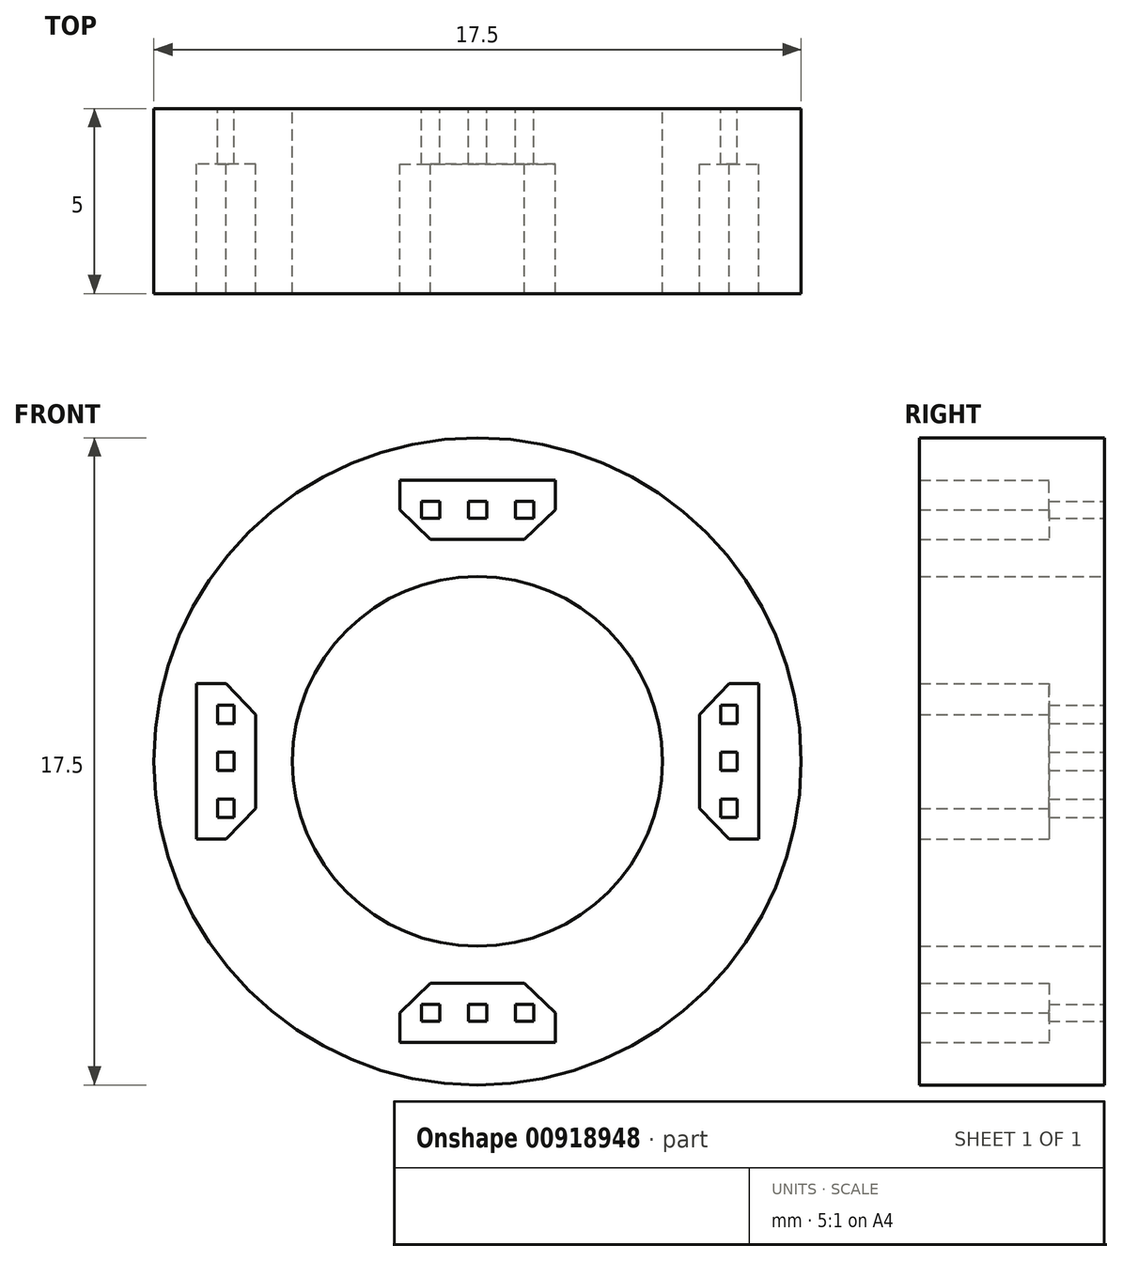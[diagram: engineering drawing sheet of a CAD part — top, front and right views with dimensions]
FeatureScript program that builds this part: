
annotation { "Feature Type Name" : "Feature", "Feature Type Description" : "" }
export const myFeature = defineFeature(function(context is Context, id is Id, definition is map)
    precondition{}
    {
        {
            var Q0;
            Q0=qCreatedBy(makeId("Front.planeOp"),FACE);
            var sketch = newSketch(context, id + "F0", { "sketchPlane" : qUnion([Q0])});
            skLineSegment(sketch, "E0", {"start": v(-2.1, 7.6) * mm, "end": v(2.1, 7.6) * mm});
            skLineSegment(sketch, "E1", {"start": v(2.1, 7.6) * mm, "end": v(2.1, 6.8) * mm});
            skLineSegment(sketch, "E2", {"start": v(2.1, 6.8) * mm, "end": v(1.27, 6) * mm});
            skLineSegment(sketch, "E3", {"start": v(1.27, 6) * mm, "end": v(-1.27, 6) * mm});
            skLineSegment(sketch, "E4", {"start": v(-1.27, 6) * mm, "end": v(-2.1, 6.8) * mm});
            skLineSegment(sketch, "E5", {"start": v(-2.1, 6.8) * mm, "end": v(-2.1, 7.6) * mm});
            skPoint(sketch, "E6", {"position": v(0, 7.6) * mm});
            skPoint(sketch, "E7", {"position": v(0, 6) * mm});
            skLineSegment(sketch, "E8", {"start": v(-2.1, 6.8) * mm, "end": v(2.1, 6.8) * mm, "construction": true});
            skLineSegment(sketch, "E9", {"start": v(0, 7.6) * mm, "end": v(0, 6) * mm, "construction": true});
            skPoint(sketch, "E10", {"position": v(0, 6.8) * mm});
            skLineSegment(sketch, "E11.bottom", {"start": v(0.25, 6.58) * mm, "end": v(-0.25, 6.58) * mm});
            skLineSegment(sketch, "E11.top", {"start": v(0.25, 7.03) * mm, "end": v(-0.25, 7.03) * mm});
            skLineSegment(sketch, "E11.left", {"start": v(0.25, 6.58) * mm, "end": v(0.25, 7.03) * mm});
            skLineSegment(sketch, "E11.right", {"start": v(-0.25, 6.58) * mm, "end": v(-0.25, 7.03) * mm});
            skLineSegment(sketch, "E12", {"start": v(1.27, 6) * mm, "end": v(1.27, 7.6) * mm, "construction": true});
            skPoint(sketch, "E13", {"position": v(1.27, 6.8) * mm});
            skLineSegment(sketch, "E14", {"start": v(-1.27, 6) * mm, "end": v(-1.27, 7.6) * mm, "construction": true});
            skPoint(sketch, "E15", {"position": v(-1.27, 6.8) * mm});
            skLineSegment(sketch, "E16", {"start": v(-1.52, 7.03) * mm, "end": v(-1.02, 7.03) * mm});
            skLineSegment(sketch, "E17", {"start": v(-1.02, 7.03) * mm, "end": v(-1.02, 6.58) * mm});
            skLineSegment(sketch, "E18", {"start": v(-1.02, 6.58) * mm, "end": v(-1.52, 6.58) * mm});
            skLineSegment(sketch, "E19", {"start": v(-1.52, 6.58) * mm, "end": v(-1.52, 7.03) * mm});
            skPoint(sketch, "E20", {"position": v(-1.27, 7.03) * mm});
            skLineSegment(sketch, "E21", {"start": v(1.52, 7.03) * mm, "end": v(1.52, 6.58) * mm});
            skLineSegment(sketch, "E22", {"start": v(1.52, 6.58) * mm, "end": v(1.02, 6.58) * mm});
            skLineSegment(sketch, "E23", {"start": v(1.02, 6.58) * mm, "end": v(1.02, 7.03) * mm});
            skLineSegment(sketch, "E24", {"start": v(1.02, 7.03) * mm, "end": v(1.52, 7.03) * mm});
            skPoint(sketch, "E25", {"position": v(1.27, 7.03) * mm});
            skPoint(sketch, "E26.1.0", {"position": v(-6.8, 1.27) * mm});
            skLineSegment(sketch, "E26.1.1", {"start": v(-6, 1.27) * mm, "end": v(-6, -1.27) * mm});
            skPoint(sketch, "E26.1.2", {"position": v(-7.03, 1.27) * mm});
            skLineSegment(sketch, "E26.1.3", {"start": v(-7.6, -2.1) * mm, "end": v(-7.6, 2.1) * mm});
            skPoint(sketch, "E26.1.4", {"position": v(-6, 0) * mm});
            skLineSegment(sketch, "E26.1.5", {"start": v(-6.8, 2.1) * mm, "end": v(-6, 1.27) * mm});
            skPoint(sketch, "E26.1.6", {"position": v(-7.6, 0) * mm});
            skLineSegment(sketch, "E26.1.7", {"start": v(-6, -1.27) * mm, "end": v(-6.8, -2.1) * mm});
            skPoint(sketch, "E26.1.8", {"position": v(-7.03, -1.27) * mm});
            skPoint(sketch, "E26.1.9", {"position": v(-6.8, -1.27) * mm});
            skLineSegment(sketch, "E26.1.10", {"start": v(-6.8, -2.1) * mm, "end": v(-7.6, -2.1) * mm});
            skLineSegment(sketch, "E26.1.11", {"start": v(-6, -1.27) * mm, "end": v(-7.6, -1.27) * mm, "construction": true});
            skLineSegment(sketch, "E26.1.12", {"start": v(-6, 1.27) * mm, "end": v(-7.6, 1.27) * mm, "construction": true});
            skLineSegment(sketch, "E26.1.13", {"start": v(-7.6, 2.1) * mm, "end": v(-6.8, 2.1) * mm});
            skPoint(sketch, "E26.1.14", {"position": v(-6.8, 0) * mm});
            skLineSegment(sketch, "E26.1.15", {"start": v(-6.8, -2.1) * mm, "end": v(-6.8, 2.1) * mm, "construction": true});
            skLineSegment(sketch, "E26.1.16", {"start": v(-7.6, 0) * mm, "end": v(-6, 0) * mm, "construction": true});
            skLineSegment(sketch, "E26.1.17", {"start": v(-6.58, -1.02) * mm, "end": v(-6.58, -1.52) * mm});
            skLineSegment(sketch, "E26.1.18", {"start": v(-7.03, -1.52) * mm, "end": v(-7.03, -1.02) * mm});
            skLineSegment(sketch, "E26.1.19", {"start": v(-6.58, 1.52) * mm, "end": v(-6.58, 1.02) * mm});
            skLineSegment(sketch, "E26.1.20", {"start": v(-7.03, -1.02) * mm, "end": v(-6.58, -1.02) * mm});
            skLineSegment(sketch, "E26.1.21", {"start": v(-6.58, 1.02) * mm, "end": v(-7.03, 1.02) * mm});
            skLineSegment(sketch, "E26.1.22", {"start": v(-7.03, 1.52) * mm, "end": v(-6.58, 1.52) * mm});
            skLineSegment(sketch, "E26.1.23", {"start": v(-7.03, 1.02) * mm, "end": v(-7.03, 1.52) * mm});
            skPoint(sketch, "E26.1.24", {"position": v(-6.8, 0) * mm});
            skLineSegment(sketch, "E26.1.25", {"start": v(-6.58, -1.52) * mm, "end": v(-7.03, -1.52) * mm});
            skLineSegment(sketch, "E26.1.26", {"start": v(-7.03, 0.25) * mm, "end": v(-7.03, -0.25) * mm});
            skLineSegment(sketch, "E26.1.27", {"start": v(-6.58, -0.25) * mm, "end": v(-7.03, -0.25) * mm});
            skLineSegment(sketch, "E26.1.28", {"start": v(-6.58, 0.25) * mm, "end": v(-7.03, 0.25) * mm});
            skLineSegment(sketch, "E26.1.29", {"start": v(-6.58, 0.25) * mm, "end": v(-6.58, -0.25) * mm});
            skPoint(sketch, "E26.2.0", {"position": v(-1.27, -6.8) * mm});
            skLineSegment(sketch, "E26.2.1", {"start": v(-1.27, -6) * mm, "end": v(1.27, -6) * mm});
            skPoint(sketch, "E26.2.2", {"position": v(-1.27, -7.03) * mm});
            skLineSegment(sketch, "E26.2.3", {"start": v(2.1, -7.6) * mm, "end": v(-2.1, -7.6) * mm});
            skPoint(sketch, "E26.2.4", {"position": v(0, -6) * mm});
            skLineSegment(sketch, "E26.2.5", {"start": v(-2.1, -6.8) * mm, "end": v(-1.27, -6) * mm});
            skPoint(sketch, "E26.2.6", {"position": v(0, -7.6) * mm});
            skLineSegment(sketch, "E26.2.7", {"start": v(1.27, -6) * mm, "end": v(2.1, -6.8) * mm});
            skPoint(sketch, "E26.2.8", {"position": v(1.27, -7.03) * mm});
            skPoint(sketch, "E26.2.9", {"position": v(1.27, -6.8) * mm});
            skLineSegment(sketch, "E26.2.10", {"start": v(2.1, -6.8) * mm, "end": v(2.1, -7.6) * mm});
            skLineSegment(sketch, "E26.2.11", {"start": v(1.27, -6) * mm, "end": v(1.27, -7.6) * mm, "construction": true});
            skLineSegment(sketch, "E26.2.12", {"start": v(-1.27, -6) * mm, "end": v(-1.27, -7.6) * mm, "construction": true});
            skLineSegment(sketch, "E26.2.13", {"start": v(-2.1, -7.6) * mm, "end": v(-2.1, -6.8) * mm});
            skPoint(sketch, "E26.2.14", {"position": v(0, -6.8) * mm});
            skLineSegment(sketch, "E26.2.15", {"start": v(2.1, -6.8) * mm, "end": v(-2.1, -6.8) * mm, "construction": true});
            skLineSegment(sketch, "E26.2.16", {"start": v(0, -7.6) * mm, "end": v(0, -6) * mm, "construction": true});
            skLineSegment(sketch, "E26.2.17", {"start": v(1.02, -6.58) * mm, "end": v(1.52, -6.58) * mm});
            skLineSegment(sketch, "E26.2.18", {"start": v(1.52, -7.03) * mm, "end": v(1.02, -7.03) * mm});
            skLineSegment(sketch, "E26.2.19", {"start": v(-1.52, -6.58) * mm, "end": v(-1.02, -6.58) * mm});
            skLineSegment(sketch, "E26.2.20", {"start": v(1.02, -7.03) * mm, "end": v(1.02, -6.58) * mm});
            skLineSegment(sketch, "E26.2.21", {"start": v(-1.02, -6.58) * mm, "end": v(-1.02, -7.03) * mm});
            skLineSegment(sketch, "E26.2.22", {"start": v(-1.52, -7.03) * mm, "end": v(-1.52, -6.58) * mm});
            skLineSegment(sketch, "E26.2.23", {"start": v(-1.02, -7.03) * mm, "end": v(-1.52, -7.03) * mm});
            skPoint(sketch, "E26.2.24", {"position": v(0, -6.8) * mm});
            skLineSegment(sketch, "E26.2.25", {"start": v(1.52, -6.58) * mm, "end": v(1.52, -7.03) * mm});
            skLineSegment(sketch, "E26.2.26", {"start": v(-0.25, -7.03) * mm, "end": v(0.25, -7.03) * mm});
            skLineSegment(sketch, "E26.2.27", {"start": v(0.25, -6.58) * mm, "end": v(0.25, -7.03) * mm});
            skLineSegment(sketch, "E26.2.28", {"start": v(-0.25, -6.58) * mm, "end": v(-0.25, -7.03) * mm});
            skLineSegment(sketch, "E26.2.29", {"start": v(-0.25, -6.58) * mm, "end": v(0.25, -6.58) * mm});
            skPoint(sketch, "E26.3.0", {"position": v(6.8, -1.27) * mm});
            skLineSegment(sketch, "E26.3.1", {"start": v(6, -1.27) * mm, "end": v(6, 1.27) * mm});
            skPoint(sketch, "E26.3.2", {"position": v(7.03, -1.27) * mm});
            skLineSegment(sketch, "E26.3.3", {"start": v(7.6, 2.1) * mm, "end": v(7.6, -2.1) * mm});
            skPoint(sketch, "E26.3.4", {"position": v(6, 0) * mm});
            skLineSegment(sketch, "E26.3.5", {"start": v(6.8, -2.1) * mm, "end": v(6, -1.27) * mm});
            skPoint(sketch, "E26.3.6", {"position": v(7.6, 0) * mm});
            skLineSegment(sketch, "E26.3.7", {"start": v(6, 1.27) * mm, "end": v(6.8, 2.1) * mm});
            skPoint(sketch, "E26.3.8", {"position": v(7.03, 1.27) * mm});
            skPoint(sketch, "E26.3.9", {"position": v(6.8, 1.27) * mm});
            skLineSegment(sketch, "E26.3.10", {"start": v(6.8, 2.1) * mm, "end": v(7.6, 2.1) * mm});
            skLineSegment(sketch, "E26.3.11", {"start": v(6, 1.27) * mm, "end": v(7.6, 1.27) * mm, "construction": true});
            skLineSegment(sketch, "E26.3.12", {"start": v(6, -1.27) * mm, "end": v(7.6, -1.27) * mm, "construction": true});
            skLineSegment(sketch, "E26.3.13", {"start": v(7.6, -2.1) * mm, "end": v(6.8, -2.1) * mm});
            skPoint(sketch, "E26.3.14", {"position": v(6.8, 0) * mm});
            skLineSegment(sketch, "E26.3.15", {"start": v(6.8, 2.1) * mm, "end": v(6.8, -2.1) * mm, "construction": true});
            skLineSegment(sketch, "E26.3.16", {"start": v(7.6, 0) * mm, "end": v(6, 0) * mm, "construction": true});
            skLineSegment(sketch, "E26.3.17", {"start": v(6.58, 1.02) * mm, "end": v(6.58, 1.52) * mm});
            skLineSegment(sketch, "E26.3.18", {"start": v(7.03, 1.52) * mm, "end": v(7.03, 1.02) * mm});
            skLineSegment(sketch, "E26.3.19", {"start": v(6.58, -1.52) * mm, "end": v(6.58, -1.02) * mm});
            skLineSegment(sketch, "E26.3.20", {"start": v(7.03, 1.02) * mm, "end": v(6.58, 1.02) * mm});
            skLineSegment(sketch, "E26.3.21", {"start": v(6.58, -1.02) * mm, "end": v(7.03, -1.02) * mm});
            skLineSegment(sketch, "E26.3.22", {"start": v(7.03, -1.52) * mm, "end": v(6.58, -1.52) * mm});
            skLineSegment(sketch, "E26.3.23", {"start": v(7.03, -1.02) * mm, "end": v(7.03, -1.52) * mm});
            skPoint(sketch, "E26.3.24", {"position": v(6.8, 0) * mm});
            skLineSegment(sketch, "E26.3.25", {"start": v(6.58, 1.52) * mm, "end": v(7.03, 1.52) * mm});
            skLineSegment(sketch, "E26.3.26", {"start": v(7.03, -0.25) * mm, "end": v(7.03, 0.25) * mm});
            skLineSegment(sketch, "E26.3.27", {"start": v(6.58, 0.25) * mm, "end": v(7.03, 0.25) * mm});
            skLineSegment(sketch, "E26.3.28", {"start": v(6.58, -0.25) * mm, "end": v(7.03, -0.25) * mm});
            skLineSegment(sketch, "E26.3.29", {"start": v(6.58, -0.25) * mm, "end": v(6.58, 0.25) * mm});
            skPoint(sketch, "E26.center", {"position": v(0, 0) * mm});
            skCircle(sketch, "E27", {"center": v(0, 0) * mm, "radius": 5 * mm});
            skCircle(sketch, "E28", {"center": v(0, 0) * mm, "radius": 8.75 * mm});
            skSolve(sketch);
        }
        {
            var Q0;
            Q0=makeQuery(id+"F0.imprint","IMPRINT",FACE,{"disambiguationData":[TD([[makeQuery(id+"F0.imprint","IMPRINT",EDGE,{"derivedFrom":sQuery(id+"F0.wireOp",EDGE,"E0")}),1.0]])]});
            extrude(context, id + "F1", {"entities" : qUnion([Q0]), "depth" : 5 * mm, "offsetDistance" : 25 * mm});
        }
        {
            var Q0;
            Q0=makeQuery(id+"F0.imprint","IMPRINT",FACE,{"disambiguationData":[TD([[makeQuery(id+"F0.imprint","IMPRINT",EDGE,{"derivedFrom":sQuery(id+"F0.wireOp",EDGE,"E0")}),-1.0]])]});
            var Q1;
            Q1=makeQuery(id+"F0.imprint","IMPRINT",FACE,{"disambiguationData":[TD([[makeQuery(id+"F0.imprint","IMPRINT",EDGE,{"derivedFrom":sQuery(id+"F0.wireOp",EDGE,"E26.1.1")}),-1.0]])]});
            var Q2;
            Q2=makeQuery(id+"F0.imprint","IMPRINT",FACE,{"disambiguationData":[TD([[makeQuery(id+"F0.imprint","IMPRINT",EDGE,{"derivedFrom":sQuery(id+"F0.wireOp",EDGE,"E26.2.1")}),-1.0]])]});
            var Q3;
            Q3=makeQuery(id+"F0.imprint","IMPRINT",FACE,{"disambiguationData":[TD([[makeQuery(id+"F0.imprint","IMPRINT",EDGE,{"derivedFrom":sQuery(id+"F0.wireOp",EDGE,"E26.3.1")}),-1.0]])]});
            extrude(context, id + "F2", {"entities" : qUnion([Q0, Q1, Q2, Q3]), "operationType" : NewBodyOperationType.ADD, "depth" : 1.5 * mm, "offsetDistance" : 25 * mm});
        }
    });
